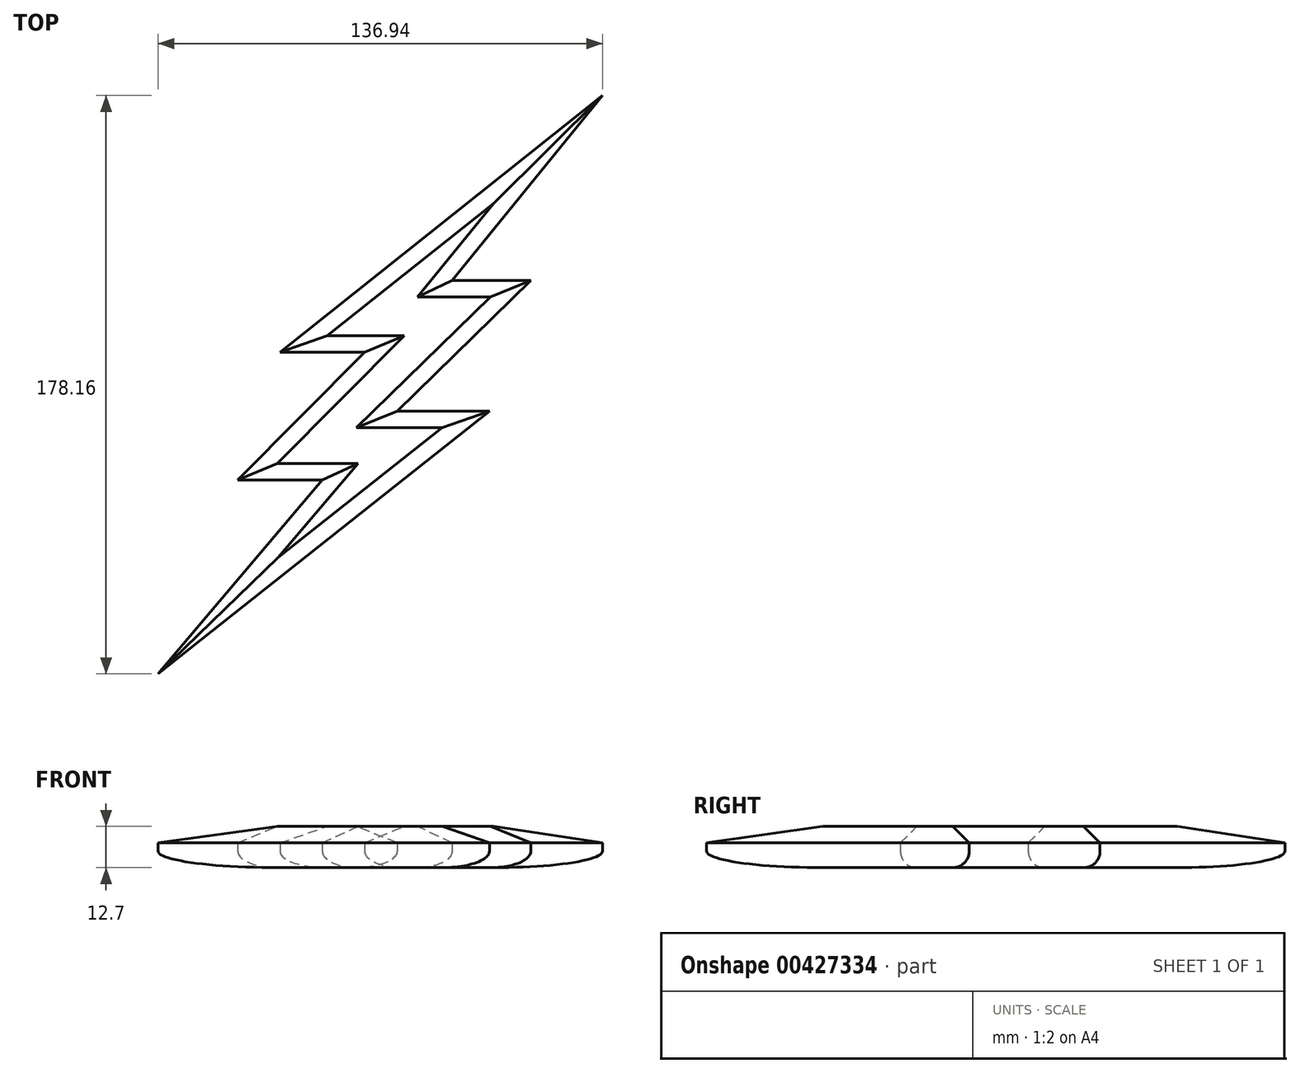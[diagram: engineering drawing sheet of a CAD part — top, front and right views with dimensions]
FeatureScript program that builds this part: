
annotation { "Feature Type Name" : "Feature", "Feature Type Description" : "" }
export const myFeature = defineFeature(function(context is Context, id is Id, definition is map)
    precondition{}
    {
        {
            var Q0;
            Q0=qCreatedBy(makeId("Top.planeOp"),FACE);
            var sketch = newSketch(context, id + "F0", { "sketchPlane" : qUnion([Q0])});
            skLineSegment(sketch, "E0", {"start": v(68.47, 89.08) * mm, "end": v(-30.9, 10) * mm});
            skLineSegment(sketch, "E1", {"start": v(-30.9, 10) * mm, "end": v(-4.85, 10) * mm});
            skLineSegment(sketch, "E2", {"start": v(-4.85, 10) * mm, "end": v(-43.93, -29.39) * mm});
            skLineSegment(sketch, "E3", {"start": v(-43.93, -29.39) * mm, "end": v(-17.88, -29.39) * mm});
            skLineSegment(sketch, "E4", {"start": v(-17.88, -29.39) * mm, "end": v(-68.47, -89.08) * mm});
            skLineSegment(sketch, "E5", {"start": v(-68.47, -89.08) * mm, "end": v(33.63, -8.18) * mm});
            skLineSegment(sketch, "E6", {"start": v(33.63, -8.18) * mm, "end": v(5.15, -8.18) * mm});
            skLineSegment(sketch, "E7", {"start": v(5.15, -8.18) * mm, "end": v(46.36, 32.12) * mm});
            skLineSegment(sketch, "E8", {"start": v(46.36, 32.12) * mm, "end": v(22.12, 32.12) * mm});
            skLineSegment(sketch, "E9", {"start": v(22.12, 32.12) * mm, "end": v(68.47, 89.08) * mm});
            skSolve(sketch);
        }
        {
            var Q0;
            Q0=makeQuery(id+"F0.imprint","IMPRINT",FACE,{"disambiguationData":[TD([[makeQuery(id+"F0.imprint","IMPRINT",EDGE,{"derivedFrom":sQuery(id+"F0.wireOp",EDGE,"E0")}),1.0]])]});
            extrude(context, id + "F1", {"entities" : qUnion([Q0]), "depth" : 12.7 * mm});
        }
        {
            var Q0;
            Q0=makeQuery(id+"F1.opExtrude","CAP_FACE",FACE,{"disambiguationData":[OSD([sQuery(id+"F0.wireOp",EDGE,"E0"),sQuery(id+"F0.wireOp",EDGE,"E1"),sQuery(id+"F0.wireOp",EDGE,"E2"),sQuery(id+"F0.wireOp",EDGE,"E3"),sQuery(id+"F0.wireOp",EDGE,"E4"),sQuery(id+"F0.wireOp",EDGE,"E5"),sQuery(id+"F0.wireOp",EDGE,"E6"),sQuery(id+"F0.wireOp",EDGE,"E7"),sQuery(id+"F0.wireOp",EDGE,"E8"),sQuery(id+"F0.wireOp",EDGE,"E9")])],"isStart":false});
            chamfer(context, id + "F2", {"entities" : qUnion([Q0]), "width" : 5.08 * mm, "tangentPropagation" : true});
        }
        {
            var Q0;
            Q0=makeQuery(id+"F1.opExtrude","CAP_FACE",FACE,{"disambiguationData":[OSD([sQuery(id+"F0.wireOp",EDGE,"E0"),sQuery(id+"F0.wireOp",EDGE,"E1"),sQuery(id+"F0.wireOp",EDGE,"E2"),sQuery(id+"F0.wireOp",EDGE,"E3"),sQuery(id+"F0.wireOp",EDGE,"E4"),sQuery(id+"F0.wireOp",EDGE,"E5"),sQuery(id+"F0.wireOp",EDGE,"E6"),sQuery(id+"F0.wireOp",EDGE,"E7"),sQuery(id+"F0.wireOp",EDGE,"E8"),sQuery(id+"F0.wireOp",EDGE,"E9")])],"isStart":true});
            fillet(context, id + "F3", {"entities" : qUnion([Q0]), "radius" : 5.08 * mm, "tangentPropagation" : true, "allowEdgeOverflow" : false});
        }
    });
